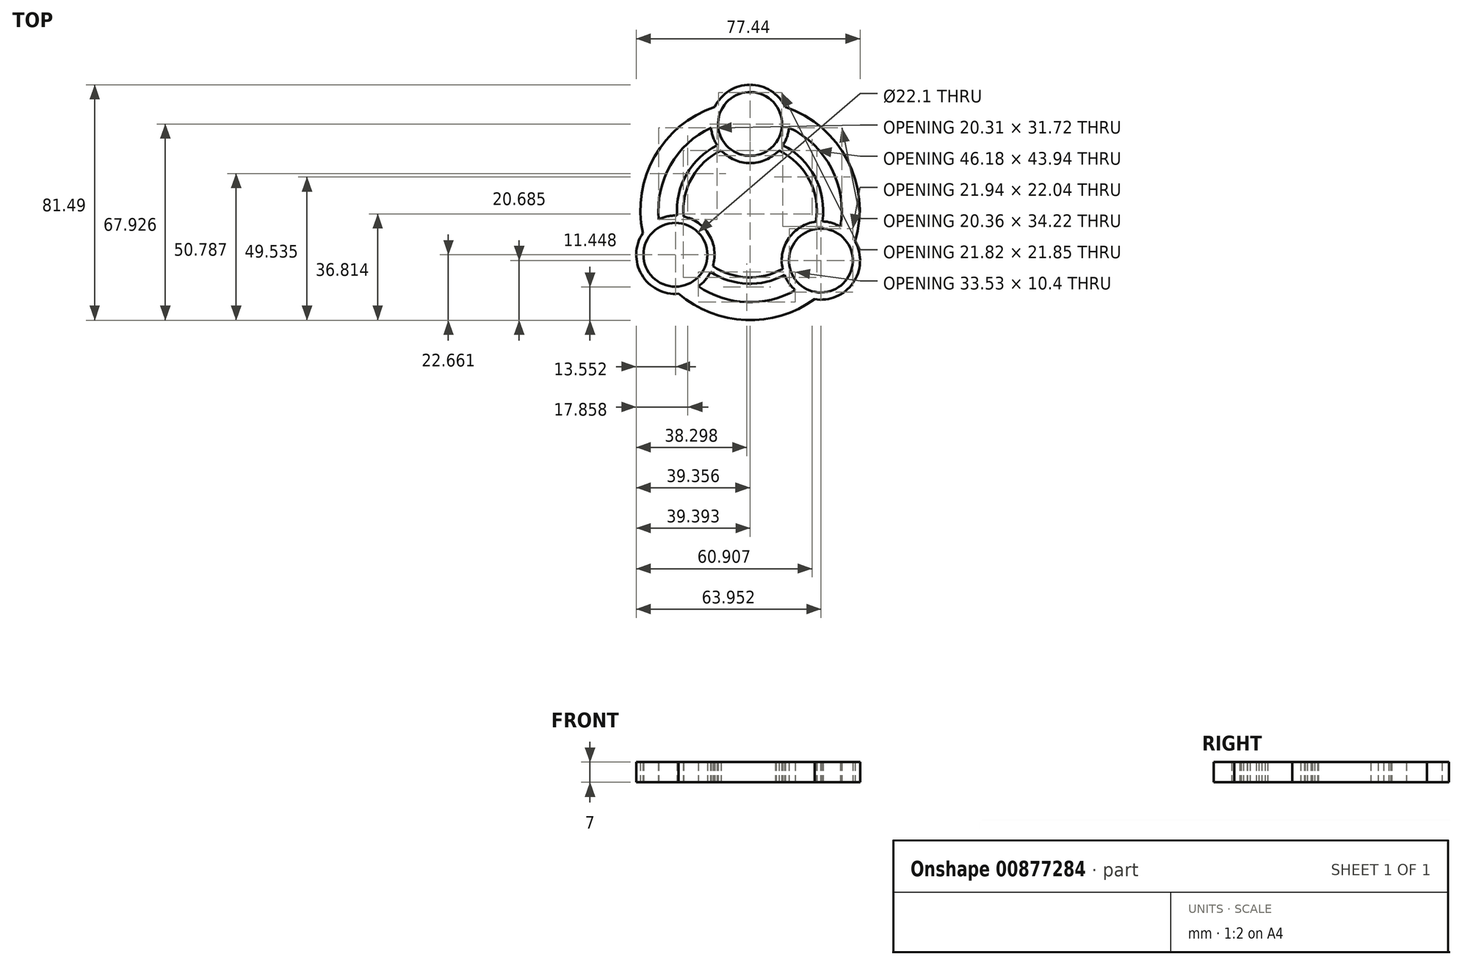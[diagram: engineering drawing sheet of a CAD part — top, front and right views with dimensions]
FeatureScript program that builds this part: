
annotation { "Feature Type Name" : "Feature", "Feature Type Description" : "" }
export const myFeature = defineFeature(function(context is Context, id is Id, definition is map)
    precondition{}
    {
        {
            var Q0;
            Q0=qCreatedBy(makeId("Top.planeOp"),FACE);
            var sketch = newSketch(context, id + "F0", { "sketchPlane" : qUnion([Q0])});
            skCircle(sketch, "E0", {"center": v(0, 0) * mm, "radius": 11.05 * mm});
            skCircle(sketch, "E1", {"center": v(0, 0) * mm, "radius": 13.55 * mm});
            skCircle(sketch, "E2", {"center": v(0, 30) * mm, "radius": 11.05 * mm});
            skCircle(sketch, "E3", {"center": v(0, 30) * mm, "radius": 13.55 * mm});
            skCircle(sketch, "E4.1.0", {"center": v(-25.82, -15.28) * mm, "radius": 13.55 * mm});
            skCircle(sketch, "E4.1.1", {"center": v(-25.82, -15.28) * mm, "radius": 11.05 * mm});
            skCircle(sketch, "E4.2.0", {"center": v(24.52, -17.29) * mm, "radius": 13.55 * mm});
            skCircle(sketch, "E4.2.1", {"center": v(24.52, -17.29) * mm, "radius": 11.05 * mm});
            skArc(sketch, "E5", {"start": v(-12.19, 35.93) * mm, "mid": v(-32.96, 18.8) * mm, "end": v(-37.12, -7.81) * mm});
            skArc(sketch, "E6", {"start": v(-13.49, 28.7) * mm, "mid": v(-27.55, 15.71) * mm, "end": v(-31.57, -3.01) * mm});
            skArc(sketch, "E7", {"start": v(-11.48, 22.8) * mm, "mid": v(-22.18, 12.65) * mm, "end": v(-25.47, -1.73) * mm});
            skArc(sketch, "E8.trimOffspring", {"start": v(25.25, -3.76) * mm, "mid": v(22.66, 11.75) * mm, "end": v(11.48, 22.8) * mm});
            skArc(sketch, "E9.trimOffspring", {"start": v(31.23, -5.52) * mm, "mid": v(28.16, 14.6) * mm, "end": v(13.49, 28.7) * mm});
            skArc(sketch, "E10.trimOffspring", {"start": v(36.38, -10.74) * mm, "mid": v(33.68, 17.46) * mm, "end": v(12.19, 35.93) * mm});
            skArc(sketch, "E11.trimOffspring", {"start": v(-17.84, -26.23) * mm, "mid": v(-1.26, -31.7) * mm, "end": v(15.7, -27.56) * mm});
            skArc(sketch, "E12.trimOffspring", {"start": v(-13.78, -21.5) * mm, "mid": v(-1.02, -25.5) * mm, "end": v(12.02, -22.52) * mm});
            skArc(sketch, "E13.trimOffspring", {"start": v(-24.71, -28.78) * mm, "mid": v(-1.51, -37.9) * mm, "end": v(22.34, -30.66) * mm});
            skSolve(sketch);
        }
        {
            var Q0;
            Q0 = qSketchRegion(id + "F0", true);
            extrude(context, id + "F1", {"entities" : qUnion([Q0]), "depth" : 7 * mm, "offsetDistance" : 25 * mm});
        }
        {
            var Q0;
            Q0=qCreatedBy(makeId("Top.planeOp"),FACE);
            var sketch = newSketch(context, id + "F2", { "sketchPlane" : qUnion([Q0])});
            skArc(sketch, "E14", {"start": v(24.52, -6.24) * mm, "mid": v(22.46, 11.65) * mm, "end": v(9.02, 23.64) * mm});
            skArc(sketch, "E15", {"start": v(22.19, -6.49) * mm, "mid": v(20.52, 10.63) * mm, "end": v(7.5, 21.87) * mm});
            skArc(sketch, "E16.trimOffspring", {"start": v(-15, -17.59) * mm, "mid": v(-0.93, -23.1) * mm, "end": v(13.54, -18.74) * mm});
            skArc(sketch, "E17.trimOffspring", {"start": v(-15.73, -19.83) * mm, "mid": v(-1, -25.29) * mm, "end": v(14.11, -21) * mm});
            skArc(sketch, "E18.trimOffspring", {"start": v(-7.52, 21.86) * mm, "mid": v(-20.07, 11.47) * mm, "end": v(-22.65, -4.6) * mm});
            skArc(sketch, "E19.trimOffspring", {"start": v(-9.06, 23.63) * mm, "mid": v(-21.95, 12.6) * mm, "end": v(-24.97, -4.1) * mm});
            skLineSegment(sketch, "E20", {"start": v(-24.97, -4.1) * mm, "end": v(-22.65, -4.6) * mm});
            skArc(sketch, "E21", {"start": v(7.5, 21.87) * mm, "mid": v(8.32, 22.7) * mm, "end": v(9.02, 23.64) * mm});
            skArc(sketch, "E22", {"start": v(24.52, -6.24) * mm, "mid": v(23.34, -6.27) * mm, "end": v(22.19, -6.49) * mm});
            skArc(sketch, "E23", {"start": v(13.54, -18.74) * mm, "mid": v(13.71, -19.9) * mm, "end": v(14.11, -21) * mm});
            skArc(sketch, "E24", {"start": v(-15.73, -19.83) * mm, "mid": v(-15.24, -18.75) * mm, "end": v(-15, -17.59) * mm});
            skArc(sketch, "E25", {"start": v(-9.06, 23.63) * mm, "mid": v(-8.36, 22.68) * mm, "end": v(-7.52, 21.86) * mm});
            skSolve(sketch);
        }
        {
            var Q0;
            Q0 = qSketchRegion(id + "F2", true);
            extrude(context, id + "F3", {"entities" : qUnion([Q0]), "operationType" : NewBodyOperationType.ADD, "depth" : 7 * mm, "offsetDistance" : 25 * mm});
        }
        {
            var Q0;
            Q0 = qSketchRegion(id + "F2", true);
            extrude(context, id + "F4", {"entities" : qUnion([Q0]), "operationType" : NewBodyOperationType.ADD, "depth" : 7 * mm, "offsetDistance" : 25 * mm});
        }
    });
